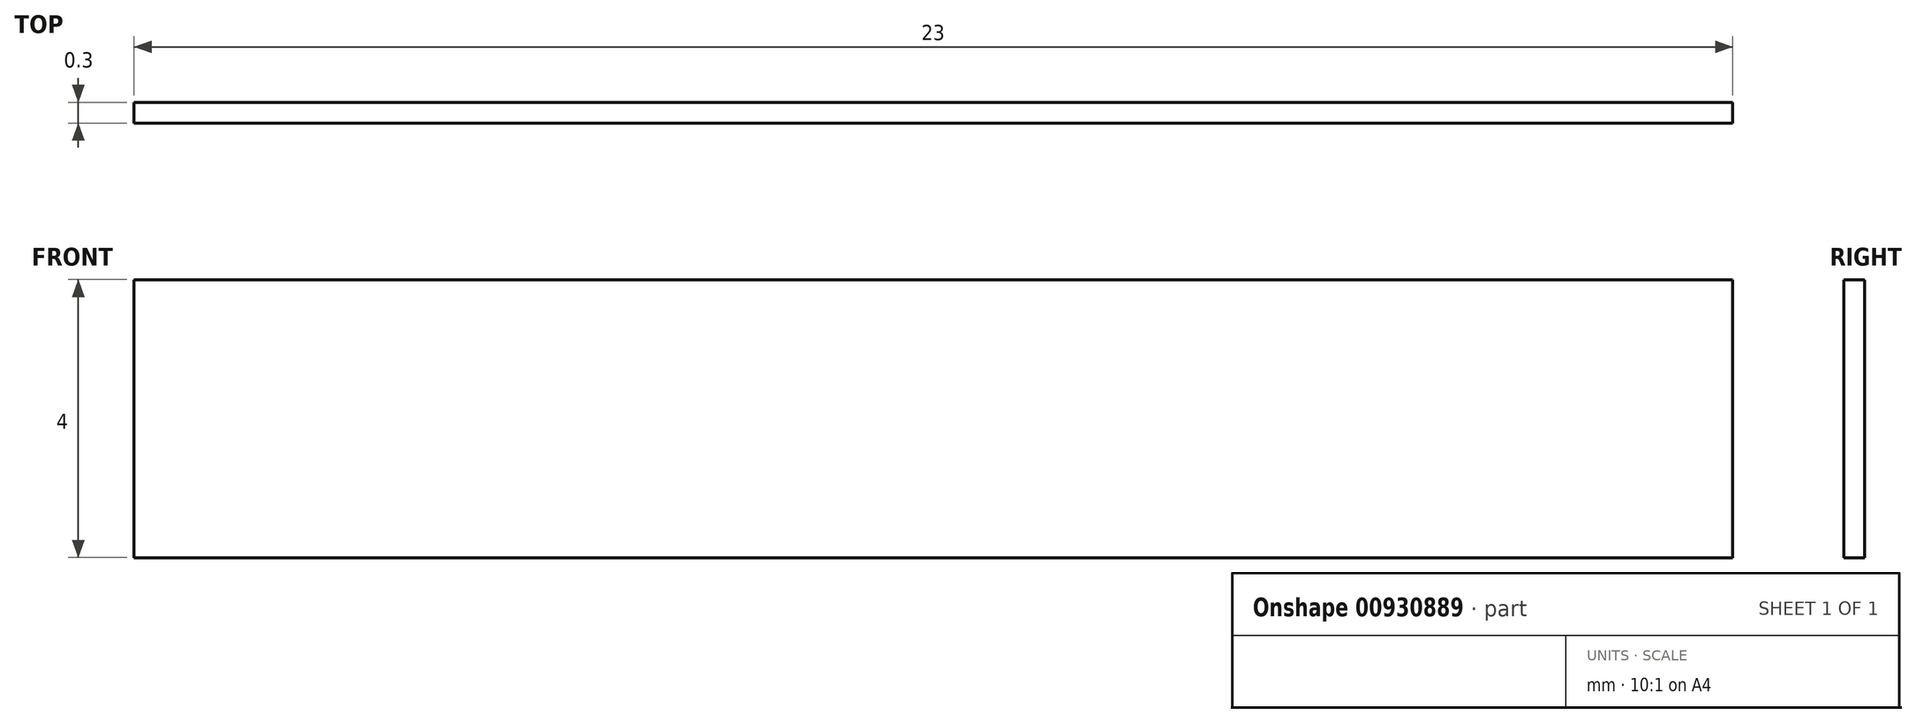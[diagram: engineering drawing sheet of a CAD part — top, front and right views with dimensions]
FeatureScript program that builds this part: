
annotation { "Feature Type Name" : "Feature", "Feature Type Description" : "" }
export const myFeature = defineFeature(function(context is Context, id is Id, definition is map)
    precondition{}
    {
        {
            var Q0;
            Q0=qCreatedBy(makeId("Front.planeOp"),FACE);
            var sketch = newSketch(context, id + "F0", { "sketchPlane" : qUnion([Q0])});
            skLineSegment(sketch, "E0.bottom", {"start": v(11.5, 2.68) * mm, "end": v(-11.5, 2.68) * mm});
            skLineSegment(sketch, "E0.top", {"start": v(11.5, -1.32) * mm, "end": v(-11.5, -1.32) * mm});
            skLineSegment(sketch, "E0.left", {"start": v(11.5, 2.68) * mm, "end": v(11.5, -1.32) * mm});
            skLineSegment(sketch, "E0.right", {"start": v(-11.5, 2.68) * mm, "end": v(-11.5, -1.32) * mm});
            skPoint(sketch, "E0.middle", {"position": v(0, 0.68) * mm});
            skSolve(sketch);
        }
        {
            var Q0;
            Q0=makeQuery(id+"F0.imprint","IMPRINT",FACE,{"disambiguationData":[TD([[makeQuery(id+"F0.imprint","IMPRINT",EDGE,{"derivedFrom":sQuery(id+"F0.wireOp",EDGE,"E0.bottom")}),1.0]])]});
            extrude(context, id + "F1", {"entities" : qUnion([Q0]), "depth" : .30 * mm, "offsetDistance" : 25 * mm});
        }
    });
